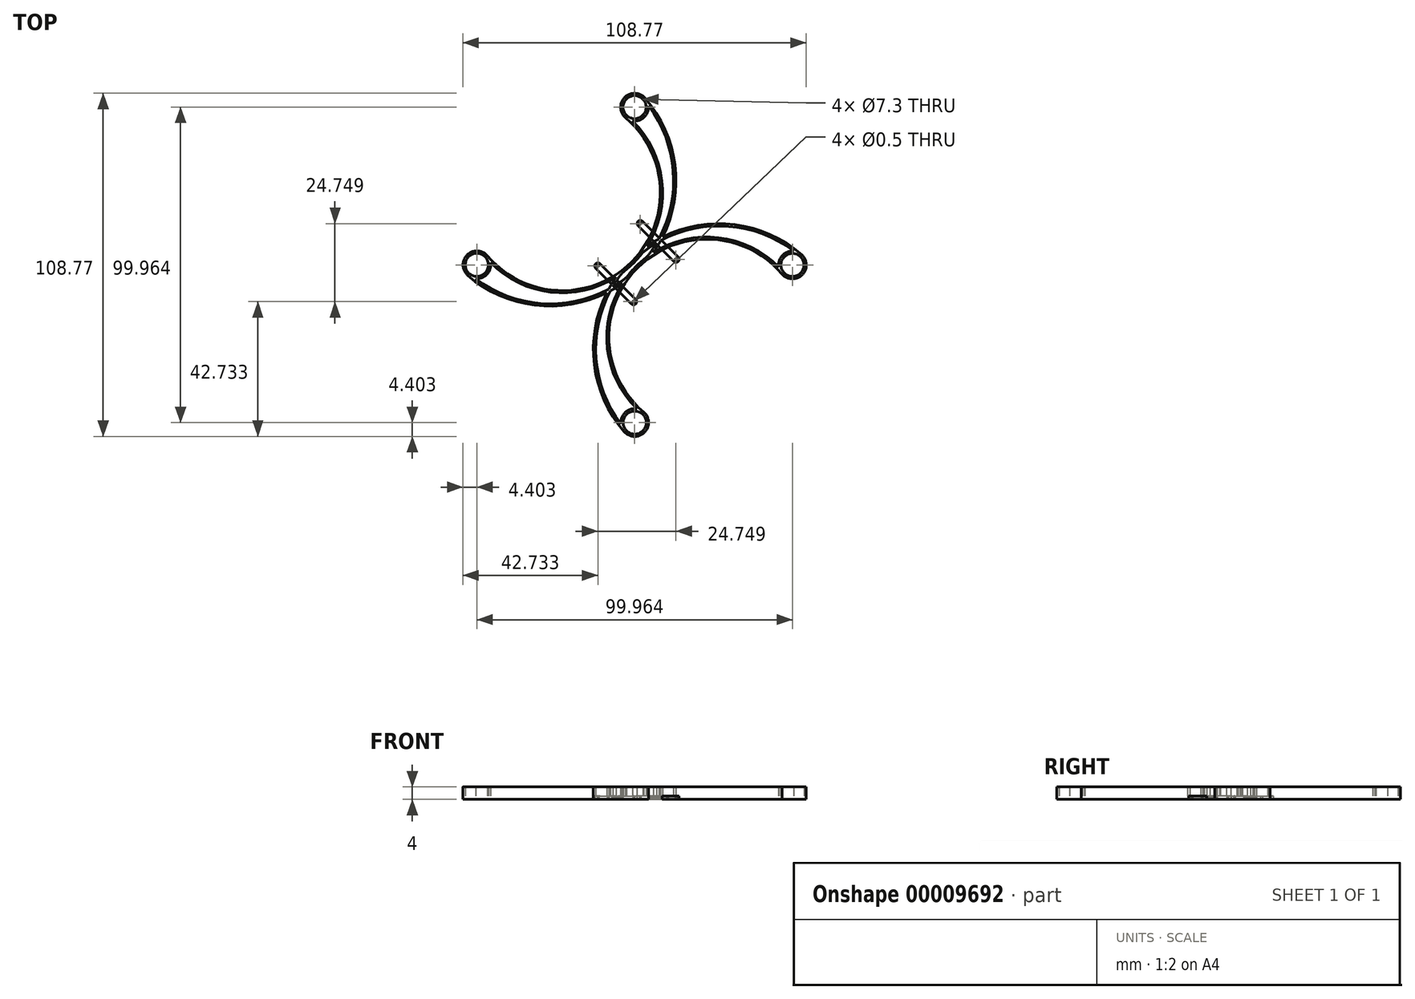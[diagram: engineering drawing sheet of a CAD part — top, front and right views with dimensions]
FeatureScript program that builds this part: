
annotation { "Feature Type Name" : "Feature", "Feature Type Description" : "" }
export const myFeature = defineFeature(function(context is Context, id is Id, definition is map)
    precondition{}
    {
        {
            var Q0;
            Q0=qCreatedBy(makeId("Top.planeOp"),FACE);
            var sketch = newSketch(context, id + "F0", { "sketchPlane" : qUnion([Q0])});
            skCircle(sketch, "E0.3.0", {"center": v(-0.04, 49.97) * mm, "radius": 3.65 * mm});
            skCircle(sketch, "E1.1.0", {"center": v(-50, 0) * mm, "radius": 3.65 * mm});
            skArc(sketch, "E2", {"start": v(-46.7, 2.9) * mm, "mid": v(-0.97, 0.94) * mm, "end": v(-2.94, 46.66) * mm});
            skArc(sketch, "E3", {"start": v(-52.88, -3.32) * mm, "mid": v(-31.7, -12.79) * mm, "end": v(-8.83, -8.83) * mm});
            skArc(sketch, "E4.trimOffspring", {"start": v(8.8, 8.8) * mm, "mid": v(12.75, 31.66) * mm, "end": v(3.28, 52.86) * mm});
            skPoint(sketch, "E5.orphan", {"position": v(-52.38, -2.74) * mm});
            skPoint(sketch, "E6.orphan", {"position": v(-47.27, 2.4) * mm});
            skPoint(sketch, "E7.orphan", {"position": v(-2.4, 47.27) * mm});
            skPoint(sketch, "E8.orphan", {"position": v(2.74, 52.38) * mm});
            skArc(sketch, "E9.trimOffspring", {"start": v(-10.4, -5.66) * mm, "mid": v(-10.37, -5.65) * mm, "end": v(-10.34, -5.64) * mm});
            skArc(sketch, "E10.trimOffspring", {"start": v(-10.35, -5.7) * mm, "mid": v(-10.37, -5.68) * mm, "end": v(-10.4, -5.66) * mm});
            skArc(sketch, "E11.0", {"start": v(-45.65, 0.7) * mm, "mid": v(-26.59, -8.65) * mm, "end": v(-5.89, -3.9) * mm});
            skArc(sketch, "E12.0", {"start": v(-50.4, -4.38) * mm, "mid": v(-30.32, -12.18) * mm, "end": v(-9.16, -8.16) * mm});
            skArc(sketch, "E13.0", {"start": v(-9.16, -8.16) * mm, "mid": v(-8.7, -7.92) * mm, "end": v(-8.22, -7.67) * mm});
            skArc(sketch, "E14.0", {"start": v(-46.7, 2.9) * mm, "mid": v(-53.12, 3.1) * mm, "end": v(-52.88, -3.32) * mm});
            skArc(sketch, "E15.0", {"start": v(3.28, 52.86) * mm, "mid": v(-3.15, 53.09) * mm, "end": v(-2.94, 46.66) * mm});
            skArc(sketch, "E16.trimOffspring", {"start": v(-50.4, -4.38) * mm, "mid": v(-46.78, -3) * mm, "end": v(-45.65, 0.7) * mm});
            skArc(sketch, "E17.trimOffspring", {"start": v(-0.75, 45.62) * mm, "mid": v(2.96, 46.75) * mm, "end": v(4.34, 50.36) * mm});
            skArc(sketch, "E18.trimOffspring", {"start": v(-4.2, -2.75) * mm, "mid": v(-0.57, 0.34) * mm, "end": v(2.56, 3.94) * mm});
            skArc(sketch, "E19.MirrorCS", {"start": v(-5.7, -10.35) * mm, "mid": v(-5.68, -10.37) * mm, "end": v(-5.66, -10.4) * mm});
            skArc(sketch, "E20.MirrorCS", {"start": v(45.62, -0.75) * mm, "mid": v(46.75, 2.96) * mm, "end": v(50.36, 4.34) * mm});
            skArc(sketch, "E21.MirrorCS", {"start": v(-3.32, -52.88) * mm, "mid": v(-12.79, -31.7) * mm, "end": v(-8.83, -8.83) * mm});
            skPoint(sketch, "E22.MirrorP", {"position": v(52.38, 2.74) * mm});
            skArc(sketch, "E23.MirrorCS", {"start": v(8.8, 8.8) * mm, "mid": v(31.66, 12.75) * mm, "end": v(52.86, 3.28) * mm});
            skArc(sketch, "E24.MirrorCS", {"start": v(-2.75, -4.2) * mm, "mid": v(0.34, -0.57) * mm, "end": v(3.94, 2.56) * mm});
            skArc(sketch, "E25.MirrorCS", {"start": v(-5.66, -10.4) * mm, "mid": v(-5.65, -10.37) * mm, "end": v(-5.64, -10.34) * mm});
            skArc(sketch, "E26.MirrorCS", {"start": v(0.7, -45.65) * mm, "mid": v(-8.65, -26.59) * mm, "end": v(-3.9, -5.89) * mm});
            skArc(sketch, "E27.MirrorCS", {"start": v(-4.38, -50.4) * mm, "mid": v(-12.18, -30.32) * mm, "end": v(-8.16, -9.16) * mm});
            skArc(sketch, "E28.MirrorCS", {"start": v(-4.38, -50.4) * mm, "mid": v(-3, -46.78) * mm, "end": v(0.7, -45.65) * mm});
            skPoint(sketch, "E29.MirrorP", {"position": v(2.4, -47.27) * mm});
            skPoint(sketch, "E30.MirrorP", {"position": v(-2.74, -52.38) * mm});
            skCircle(sketch, "E31.MirrorC", {"center": v(0, -50) * mm, "radius": 3.65 * mm});
            skArc(sketch, "E32.MirrorCS", {"start": v(52.86, 3.28) * mm, "mid": v(53.09, -3.15) * mm, "end": v(46.66, -2.94) * mm});
            skCircle(sketch, "E33.MirrorC", {"center": v(49.97, -0.04) * mm, "radius": 3.65 * mm});
            skArc(sketch, "E34.MirrorCS", {"start": v(2.9, -46.7) * mm, "mid": v(0.94, -0.97) * mm, "end": v(46.66, -2.94) * mm});
            skArc(sketch, "E35.MirrorCS", {"start": v(-8.16, -9.16) * mm, "mid": v(-7.92, -8.7) * mm, "end": v(-7.67, -8.22) * mm});
            skArc(sketch, "E36.MirrorCS", {"start": v(2.9, -46.7) * mm, "mid": v(3.1, -53.12) * mm, "end": v(-3.32, -52.88) * mm});
            skPoint(sketch, "E37.MirrorP", {"position": v(47.27, -2.4) * mm});
            skArc(sketch, "E38.trimOffspring", {"start": v(3.87, 5.85) * mm, "mid": v(5.72, 7.07) * mm, "end": v(7.63, 8.19) * mm});
            skArc(sketch, "E39.trimOffspring", {"start": v(5.85, 3.87) * mm, "mid": v(7.07, 5.72) * mm, "end": v(8.19, 7.63) * mm});
            skArc(sketch, "E40.trimOffspring", {"start": v(-8.22, -7.67) * mm, "mid": v(-7.1, -5.75) * mm, "end": v(-5.89, -3.9) * mm});
            skArc(sketch, "E41.trimOffspring", {"start": v(-6.95, -6.95) * mm, "mid": v(-5.54, -4.72) * mm, "end": v(-3.97, -2.6) * mm});
            skArc(sketch, "E42.trimOffspring", {"start": v(-7.67, -8.22) * mm, "mid": v(-5.75, -7.1) * mm, "end": v(-3.9, -5.89) * mm});
            skArc(sketch, "E43.trimOffspring", {"start": v(-6.95, -6.95) * mm, "mid": v(-4.72, -5.54) * mm, "end": v(-2.6, -3.97) * mm});
            skArc(sketch, "E44.trimOffspring", {"start": v(2.56, 3.94) * mm, "mid": v(4.69, 5.5) * mm, "end": v(6.92, 6.92) * mm});
            skArc(sketch, "E45.trimOffspring", {"start": v(3.94, 2.56) * mm, "mid": v(5.5, 4.69) * mm, "end": v(6.92, 6.92) * mm});
            skArc(sketch, "E46.trimOffspring", {"start": v(3.87, 5.85) * mm, "mid": v(8.62, 26.56) * mm, "end": v(-0.75, 45.62) * mm});
            skArc(sketch, "E47.trimOffspring", {"start": v(7.63, 8.19) * mm, "mid": v(12.2, 29.76) * mm, "end": v(4.34, 50.36) * mm});
            skArc(sketch, "E48.trimOffspring", {"start": v(8.19, 7.63) * mm, "mid": v(29.76, 12.2) * mm, "end": v(50.36, 4.34) * mm});
            skArc(sketch, "E49.trimOffspring", {"start": v(5.85, 3.87) * mm, "mid": v(26.56, 8.62) * mm, "end": v(45.62, -0.75) * mm});
            skSolve(sketch);
        }
        {
            var Q0;
            Q0=qCreatedBy(makeId("Top.planeOp"),FACE);
            var sketch = newSketch(context, id + "F1", { "sketchPlane" : qUnion([Q0])});
            skPoint(sketch, "E50", {"position": v(13.08, 1.77) * mm});
            skPoint(sketch, "E51", {"position": v(-11.67, -0.35) * mm});
            skLineSegment(sketch, "E52.0", {"start": v(-12.37, -1.06) * mm, "end": v(-6.72, -6.72) * mm});
            skLineSegment(sketch, "E53.MirrorCS", {"start": v(-10.96, 0.35) * mm, "end": v(-5.3, -5.3) * mm});
            skLineSegment(sketch, "E54.0", {"start": v(13.79, 2.47) * mm, "end": v(8.13, 8.13) * mm});
            skLineSegment(sketch, "E55.MirrorCS", {"start": v(12.37, 1.06) * mm, "end": v(6.72, 6.72) * mm});
            skArc(sketch, "E56", {"start": v(-10.96, 0.35) * mm, "mid": v(-12.37, 0.35) * mm, "end": v(-12.37, -1.06) * mm});
            skArc(sketch, "E57", {"start": v(12.37, 1.06) * mm, "mid": v(13.79, 1.06) * mm, "end": v(13.79, 2.47) * mm});
            skCircle(sketch, "E58", {"center": v(-11.67, -0.35) * mm, "radius": 0.25 * mm});
            skCircle(sketch, "E59", {"center": v(13.08, 1.77) * mm, "radius": 0.25 * mm});
            skLineSegment(sketch, "E60.MirrorCS", {"start": v(1.06, 12.37) * mm, "end": v(6.72, 6.72) * mm});
            skLineSegment(sketch, "E61.MirrorCS", {"start": v(2.47, 13.79) * mm, "end": v(8.13, 8.13) * mm});
            skArc(sketch, "E62.MirrorCS", {"start": v(1.06, 12.37) * mm, "mid": v(1.06, 13.79) * mm, "end": v(2.47, 13.79) * mm});
            skLineSegment(sketch, "E63.MirrorCS", {"start": v(0.35, -10.96) * mm, "end": v(-5.3, -5.3) * mm});
            skLineSegment(sketch, "E64.MirrorCS", {"start": v(-1.06, -12.37) * mm, "end": v(-6.72, -6.72) * mm});
            skArc(sketch, "E65.MirrorCS", {"start": v(0.35, -10.96) * mm, "mid": v(0.35, -12.37) * mm, "end": v(-1.06, -12.37) * mm});
            skCircle(sketch, "E66.MirrorC", {"center": v(-0.35, -11.67) * mm, "radius": 0.25 * mm});
            skCircle(sketch, "E67.MirrorC", {"center": v(1.77, 13.08) * mm, "radius": 0.25 * mm});
            skLineSegment(sketch, "E68", {"start": v(0, 0) * mm, "end": v(-9.92, 9.92) * mm});
            skLineSegment(sketch, "E69", {"start": v(0, 0) * mm, "end": v(11.08, 11.08) * mm});
            skSolve(sketch);
        }
        {
            var Q0;
            Q0=makeQuery(id+"F0.imprint","IMPRINT",FACE,{"disambiguationData":[TD([[makeQuery(id+"F0.imprint","IMPRINT",EDGE,{"derivedFrom":sQuery(id+"F0.wireOp",EDGE,"E0.3.0")}),-1.0]])]});
            extrude(context, id + "F2", {"entities" : qUnion([Q0]), "depth" : 4 * mm});
        }
        {
            var Q0;
            Q0 = qSketchRegion(id + "F1", true);
            extrude(context, id + "F3", {"entities" : qUnion([Q0]), "operationType" : NewBodyOperationType.ADD, "depth" : 1 * mm});
        }
    });
